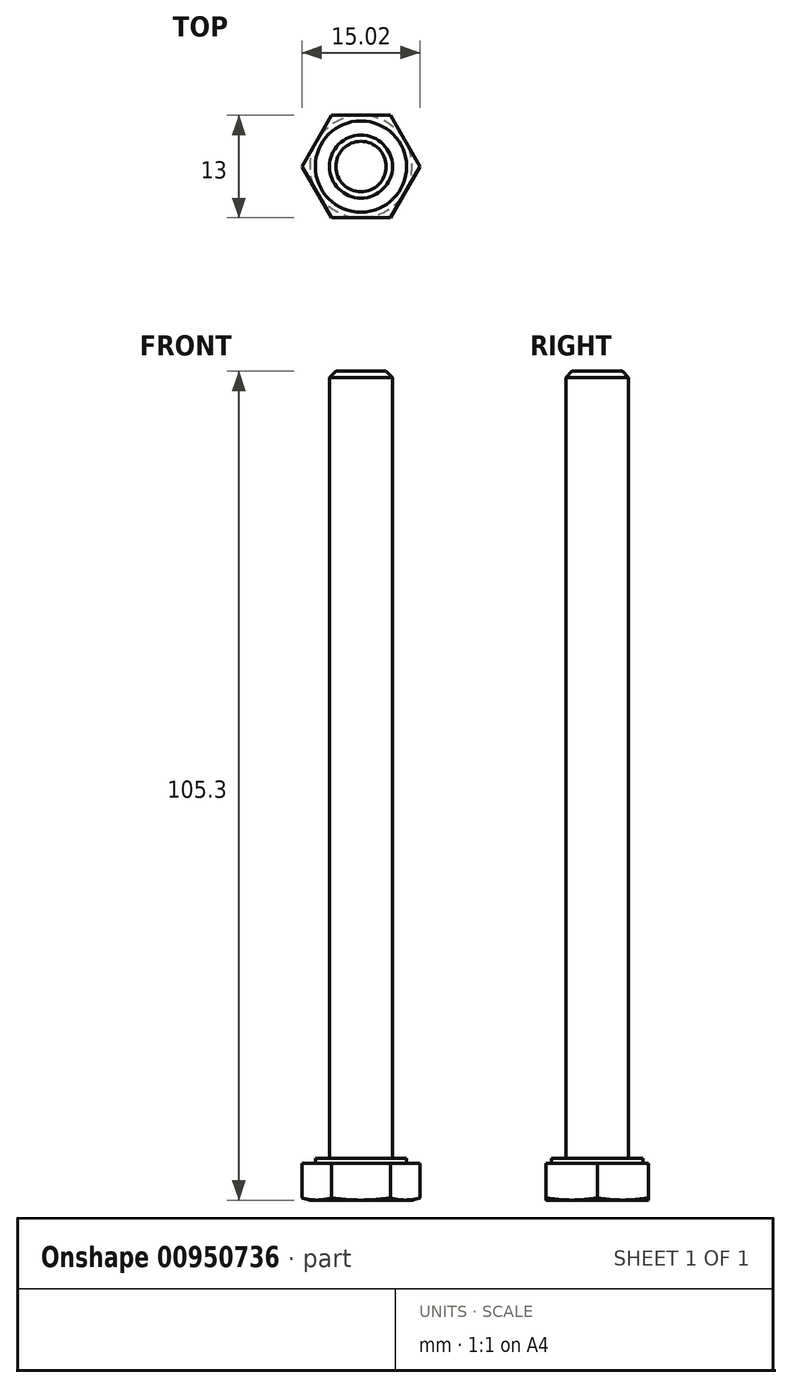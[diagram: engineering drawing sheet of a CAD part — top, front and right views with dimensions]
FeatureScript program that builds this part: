
annotation { "Feature Type Name" : "Feature", "Feature Type Description" : "" }
export const myFeature = defineFeature(function(context is Context, id is Id, definition is map)
    precondition{}
    {
        {
            var Q0;
            Q0=qCreatedBy(makeId("Top.planeOp"),FACE);
            var sketch = newSketch(context, id + "F0", { "sketchPlane" : qUnion([Q0])});
            skCircle(sketch, "E0.cCircle", {"center": v(0, 0) * mm, "radius": 6.5 * mm, "construction": true});
            skLineSegment(sketch, "E0.0", {"start": v(3.75, -6.5) * mm, "end": v(-3.75, -6.5) * mm});
            skLineSegment(sketch, "E0.1", {"start": v(-3.75, -6.5) * mm, "end": v(-7.5, 0) * mm});
            skLineSegment(sketch, "E0.2", {"start": v(-7.5, 0) * mm, "end": v(-3.75, 6.5) * mm});
            skLineSegment(sketch, "E0.3", {"start": v(-3.75, 6.5) * mm, "end": v(3.75, 6.5) * mm});
            skLineSegment(sketch, "E0.4", {"start": v(3.75, 6.5) * mm, "end": v(7.5, 0) * mm});
            skLineSegment(sketch, "E0.5", {"start": v(7.5, 0) * mm, "end": v(3.75, -6.5) * mm});
            skPoint(sketch, "E0.0.midPoint", {"position": v(0, -6.5) * mm});
            skSolve(sketch);
        }
        {
            var Q0;
            Q0=qSketchRegion(id+"F0",true);
            extrude(context, id + "F1", {"entities" : qUnion([Q0]), "depth" : 4.7 * mm, "offsetDistance" : 25 * mm});
        }
        {
            var Q0;
            Q0=qCreatedBy(makeId("Front.planeOp"),FACE);
            var sketch = newSketch(context, id + "F2", { "sketchPlane" : qUnion([Q0])});
            skLineSegment(sketch, "E1", {"start": v(0, -11.74) * mm, "end": v(0, 32.47) * mm, "construction": true});
            skLineSegment(sketch, "E2", {"start": v(-6.5, 0) * mm, "end": v(-7.5, 0.27) * mm});
            skLineSegment(sketch, "E3", {"start": v(-7.5, 0.27) * mm, "end": v(-7.5, 0) * mm});
            skLineSegment(sketch, "E4", {"start": v(-7.5, 0) * mm, "end": v(-6.5, 0) * mm});
            skSolve(sketch);
        }
        {
            var Q0;
            Q0=qSketchRegion(id+"F2",true);
            var Q1;
            Q1=sQuery(id+"F2.wireOp",EDGE,"E1");
            revolve(context, id + "F3", {"operationType" : NewBodyOperationType.REMOVE, "surfaceOperationType" : NewSurfaceOperationType.NEW, "entities" : qUnion([Q0]), "axis" : qUnion([Q1]), "revolveType" : RevolveType.FULL, "oppositeDirection" : true});
        }
        {
            var Q0;
            Q0=makeQuery(id+"F1.opExtrude","CAP_FACE",FACE,{"disambiguationData":[OSD([sQuery(id+"F0.wireOp",EDGE,"E0.0"),sQuery(id+"F0.wireOp",EDGE,"E0.1"),sQuery(id+"F0.wireOp",EDGE,"E0.2"),sQuery(id+"F0.wireOp",EDGE,"E0.3"),sQuery(id+"F0.wireOp",EDGE,"E0.4"),sQuery(id+"F0.wireOp",EDGE,"E0.5")])],"isStart":false});
            var sketch = newSketch(context, id + "F4", { "sketchPlane" : qUnion([Q0])});
            skCircle(sketch, "E5", {"center": v(0, 0) * mm, "radius": 5.8 * mm});
            skSolve(sketch);
        }
        {
            var Q0;
            Q0=qSketchRegion(id+"F4",true);
            extrude(context, id + "F5", {"entities" : qUnion([Q0]), "operationType" : NewBodyOperationType.ADD, "depth" : 0.6 * mm, "offsetDistance" : 25 * mm});
        }
        {
            var Q0;
            Q0=makeQuery(id+"F5.opExtrude","CAP_FACE",FACE,{"disambiguationData":[OSD([sQuery(id+"F4.wireOp",EDGE,"E5")])],"isStart":false});
            var sketch = newSketch(context, id + "F6", { "sketchPlane" : qUnion([Q0])});
            skCircle(sketch, "E6", {"center": v(0, 0) * mm, "radius": 4 * mm});
            skSolve(sketch);
        }
        {
            var Q0;
            Q0=qSketchRegion(id+"F6",true);
            extrude(context, id + "F7", {"entities" : qUnion([Q0]), "operationType" : NewBodyOperationType.ADD, "depth" : 100 * mm, "offsetDistance" : 25 * mm});
        }
        {
            var Q0;
            Q0=makeQuery(id+"F7.opExtrude","CAP_EDGE",EDGE,{"disambiguationData":[OSD([sQuery(id+"F6.wireOp",EDGE,"E6")])],"isStart":false});
            chamfer(context, id + "F8", {"entities" : qUnion([Q0]), "width" : 0.8 * mm, "tangentPropagation" : true});
        }
    });
